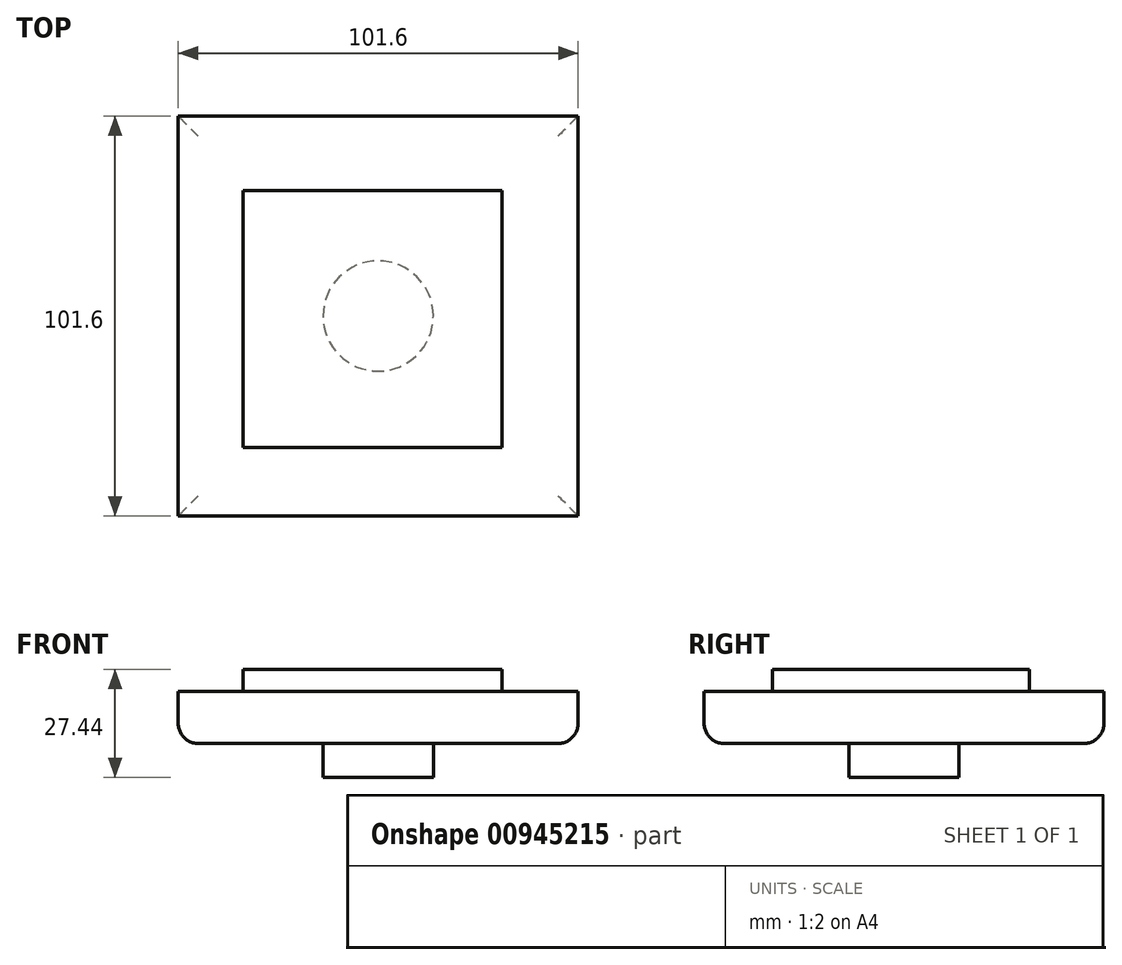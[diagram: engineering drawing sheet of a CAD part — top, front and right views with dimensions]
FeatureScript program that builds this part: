
annotation { "Feature Type Name" : "Feature", "Feature Type Description" : "" }
export const myFeature = defineFeature(function(context is Context, id is Id, definition is map)
    precondition{}
    {
        {
            var Q0;
            Q0=qCreatedBy(makeId("Top.planeOp"),FACE);
            var sketch = newSketch(context, id + "F0", { "sketchPlane" : qUnion([Q0])});
            skLineSegment(sketch, "E0.bottom", {"start": v(-50.8, 50.8) * mm, "end": v(50.8, 50.8) * mm});
            skLineSegment(sketch, "E0.top", {"start": v(-50.8, -50.8) * mm, "end": v(50.8, -50.8) * mm});
            skLineSegment(sketch, "E0.left", {"start": v(-50.8, 50.8) * mm, "end": v(-50.8, -50.8) * mm});
            skLineSegment(sketch, "E0.right", {"start": v(50.8, 50.8) * mm, "end": v(50.8, -50.8) * mm});
            skPoint(sketch, "E0.middle", {"position": v(0, 0) * mm});
            skSolve(sketch);
        }
        {
            var Q0;
            Q0 = qSketchRegion(id + "F0", true);
            extrude(context, id + "F1", {"entities" : qUnion([Q0]), "depth" : 13.2 * mm, "offsetDistance" : 25.4 * mm});
        }
        {
            var Q0;
            Q0=makeQuery(id+"F1.opExtrude","CAP_FACE",FACE,{"disambiguationData":[OSD([sQuery(id+"F0.wireOp",EDGE,"E0.bottom"),sQuery(id+"F0.wireOp",EDGE,"E0.top"),sQuery(id+"F0.wireOp",EDGE,"E0.left"),sQuery(id+"F0.wireOp",EDGE,"E0.right")])],"isStart":true});
            var sketch = newSketch(context, id + "F2", { "sketchPlane" : qUnion([Q0])});
            skCircle(sketch, "E1", {"center": v(0, 0) * mm, "radius": 14 * mm});
            skSolve(sketch);
        }
        {
            var Q0;
            Q0 = qSketchRegion(id + "F2", true);
            extrude(context, id + "F3", {"entities" : qUnion([Q0]), "operationType" : NewBodyOperationType.ADD, "depth" : 8.64 * mm, "offsetDistance" : 25.4 * mm});
        }
        {
            var Q0;
            Q0=makeQuery(id+"F3.opExtrude","CAP_FACE",FACE,{"disambiguationData":[OSD([sQuery(id+"F2.wireOp",EDGE,"E1")])],"isStart":false});
            var sketch = newSketch(context, id + "F4", { "sketchPlane" : qUnion([Q0])});
            skCircle(sketch, "E2", {"center": v(0, 0) * mm, "radius": 9.31 * mm});
            skSolve(sketch);
        }
        {
            var Q0;
            Q0=makeQuery(id+"F1.opExtrude","CAP_FACE",FACE,{"disambiguationData":[OSD([sQuery(id+"F0.wireOp",EDGE,"E0.bottom"),sQuery(id+"F0.wireOp",EDGE,"E0.top"),sQuery(id+"F0.wireOp",EDGE,"E0.left"),sQuery(id+"F0.wireOp",EDGE,"E0.right")])],"isStart":false});
            var sketch = newSketch(context, id + "F5", { "sketchPlane" : qUnion([Q0])});
            skLineSegment(sketch, "E3.bottom", {"start": v(-34.34, 31.82) * mm, "end": v(31.52, 31.82) * mm});
            skLineSegment(sketch, "E3.top", {"start": v(-34.34, -33.4) * mm, "end": v(31.52, -33.4) * mm});
            skLineSegment(sketch, "E3.left", {"start": v(-34.34, 31.82) * mm, "end": v(-34.34, -33.4) * mm});
            skLineSegment(sketch, "E3.right", {"start": v(31.52, 31.82) * mm, "end": v(31.52, -33.4) * mm});
            skSolve(sketch);
        }
        {
            var Q0;
            Q0 = qSketchRegion(id + "F5", true);
            extrude(context, id + "F6", {"entities" : qUnion([Q0]), "operationType" : NewBodyOperationType.ADD, "depth" : 5.6 * mm, "offsetDistance" : 25.4 * mm});
        }
        {
            var Q0;
            Q0=makeQuery(id+"F1.opExtrude","CAP_EDGE",EDGE,{"disambiguationData":[OSD([sQuery(id+"F0.wireOp",EDGE,"E0.left")])],"isStart":true});
            var Q1;
            Q1=makeQuery(id+"F1.opExtrude","CAP_EDGE",EDGE,{"disambiguationData":[OSD([sQuery(id+"F0.wireOp",EDGE,"E0.bottom")])],"isStart":true});
            var Q2;
            Q2=makeQuery(id+"F1.opExtrude","CAP_EDGE",EDGE,{"disambiguationData":[OSD([sQuery(id+"F0.wireOp",EDGE,"E0.right")])],"isStart":true});
            var Q3;
            Q3=makeQuery(id+"F1.opExtrude","CAP_EDGE",EDGE,{"disambiguationData":[OSD([sQuery(id+"F0.wireOp",EDGE,"E0.top")])],"isStart":true});
            fillet(context, id + "F7", {"entities" : qUnion([Q0, Q1, Q2, Q3]), "radius" : 5.08 * mm, "tangentPropagation" : true, "allowEdgeOverflow" : false});
        }
    });
